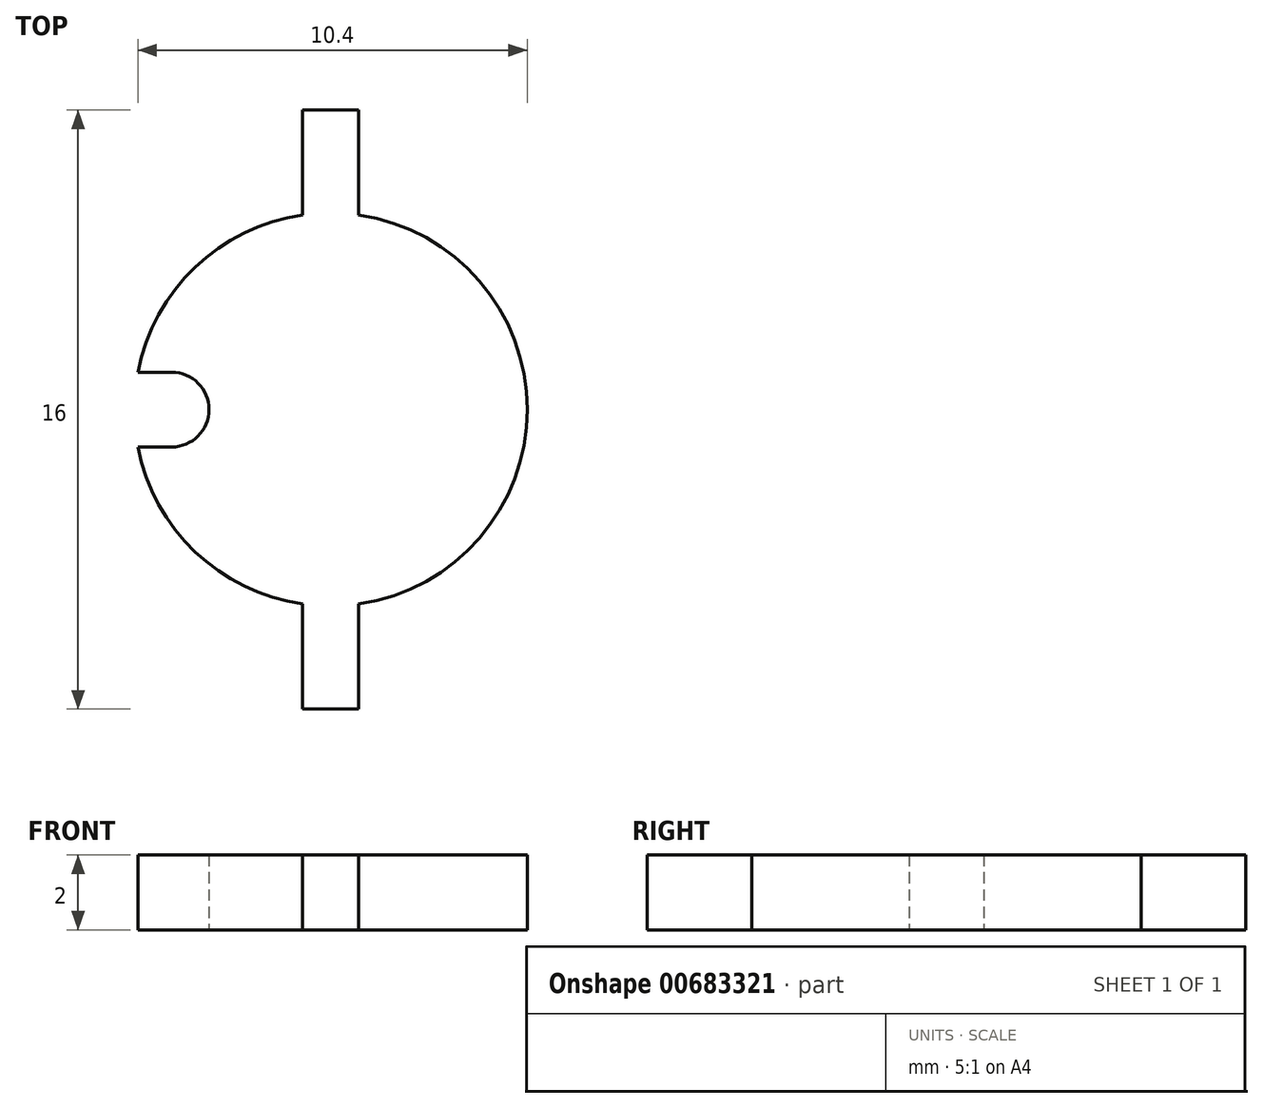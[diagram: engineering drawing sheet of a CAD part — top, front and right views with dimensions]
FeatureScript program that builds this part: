
annotation { "Feature Type Name" : "Feature", "Feature Type Description" : "" }
export const myFeature = defineFeature(function(context is Context, id is Id, definition is map)
    precondition{}
    {
        {
            var Q0;
            Q0=qCreatedBy(makeId("Top.planeOp"),FACE);
            var sketch = newSketch(context, id + "F0", { "sketchPlane" : qUnion([Q0])});
            skCircle(sketch, "E0", {"center": v(0, 0) * mm, "radius": 5.25 * mm});
            skCircle(sketch, "E1", {"center": v(0, 0) * mm, "radius": 4.25 * mm, "construction": true});
            skLineSegment(sketch, "E2", {"start": v(0, 0) * mm, "end": v(-5.25, 0) * mm, "construction": true});
            skCircle(sketch, "E3", {"center": v(-4.25, 0) * mm, "radius": 1 * mm});
            skLineSegment(sketch, "E4", {"start": v(-4.25, 0) * mm, "end": v(-4.25, 1) * mm});
            skLineSegment(sketch, "E5", {"start": v(-4.25, 1) * mm, "end": v(-6.5, 1) * mm});
            skLineSegment(sketch, "E6", {"start": v(-4.25, 0) * mm, "end": v(-4.25, -1) * mm});
            skLineSegment(sketch, "E7", {"start": v(-4.25, -1) * mm, "end": v(-7.2, -1) * mm});
            skLineSegment(sketch, "E8.bottom", {"start": v(0.75, 8) * mm, "end": v(-0.75, 8) * mm});
            skLineSegment(sketch, "E8.top", {"start": v(0.75, -8) * mm, "end": v(-0.75, -8) * mm});
            skLineSegment(sketch, "E8.left", {"start": v(0.75, 8) * mm, "end": v(0.75, -8) * mm});
            skLineSegment(sketch, "E8.right", {"start": v(-0.75, 8) * mm, "end": v(-0.75, -8) * mm});
            skSolve(sketch);
        }
        {
            var Q0;
            Q0=makeQuery(id+"F0.imprint","IMPRINT",FACE,{"disambiguationData":[TD([[makeQuery(id+"F0.imprint","IMPRINT",EDGE,{"derivedFrom":sQuery(id+"F0.wireOp",EDGE,"E0")}),1.0]])]});
            var Q1;
            {var subQ0=sQuery(id+"F0.wireOp",EDGE,"E5");var subQ6=sQuery(id+"F0.wireOp",EDGE,"E0");var subQ10=makeQuery(id+"F0.imprint","INTERSECT",VERTEX,{"derivedFrom":[subQ6,subQ0]});Q1=makeQuery(id+"F0.imprint","IMPRINT",FACE,{"disambiguationData":[TD([[makeQuery(id+"F0.imprint","IMPRINT",EDGE,{"disambiguationData":[TD([[subQ10,1.0]])],"derivedFrom":subQ6}),1.0]])]});}
            var Q2;
            {var subQ0=sQuery(id+"F0.wireOp",EDGE,"E8.left");var subQ1=sQuery(id+"F0.wireOp",EDGE,"E0");var subQ2=makeQuery(id+"F0.imprint","INTERSECT",VERTEX,{"disambiguationData":[OD(0.0)],"derivedFrom":[subQ1,subQ0]});Q2=makeQuery(id+"F0.imprint","IMPRINT",FACE,{"disambiguationData":[TD([[makeQuery(id+"F0.imprint","IMPRINT",EDGE,{"disambiguationData":[TD([[subQ2,1.0]])],"derivedFrom":subQ1}),1.0]])]});}
            var Q3;
            {var subQ5=sQuery(id+"F0.wireOp",EDGE,"E8.bottom");Q3=makeQuery(id+"F0.imprint","IMPRINT",FACE,{"disambiguationData":[TD([[makeQuery(id+"F0.imprint","IMPRINT",EDGE,{"derivedFrom":subQ5}),1.0]])]});}
            var Q4;
            {var subQ5=sQuery(id+"F0.wireOp",EDGE,"E8.top");Q4=makeQuery(id+"F0.imprint","IMPRINT",FACE,{"disambiguationData":[TD([[makeQuery(id+"F0.imprint","IMPRINT",EDGE,{"derivedFrom":subQ5}),-1.0]])]});}
            extrude(context, id + "F1", {"entities" : qUnion([Q0, Q1, Q2, Q3, Q4]), "depth" : 2 * mm, "offsetDistance" : 25 * mm});
        }
    });
